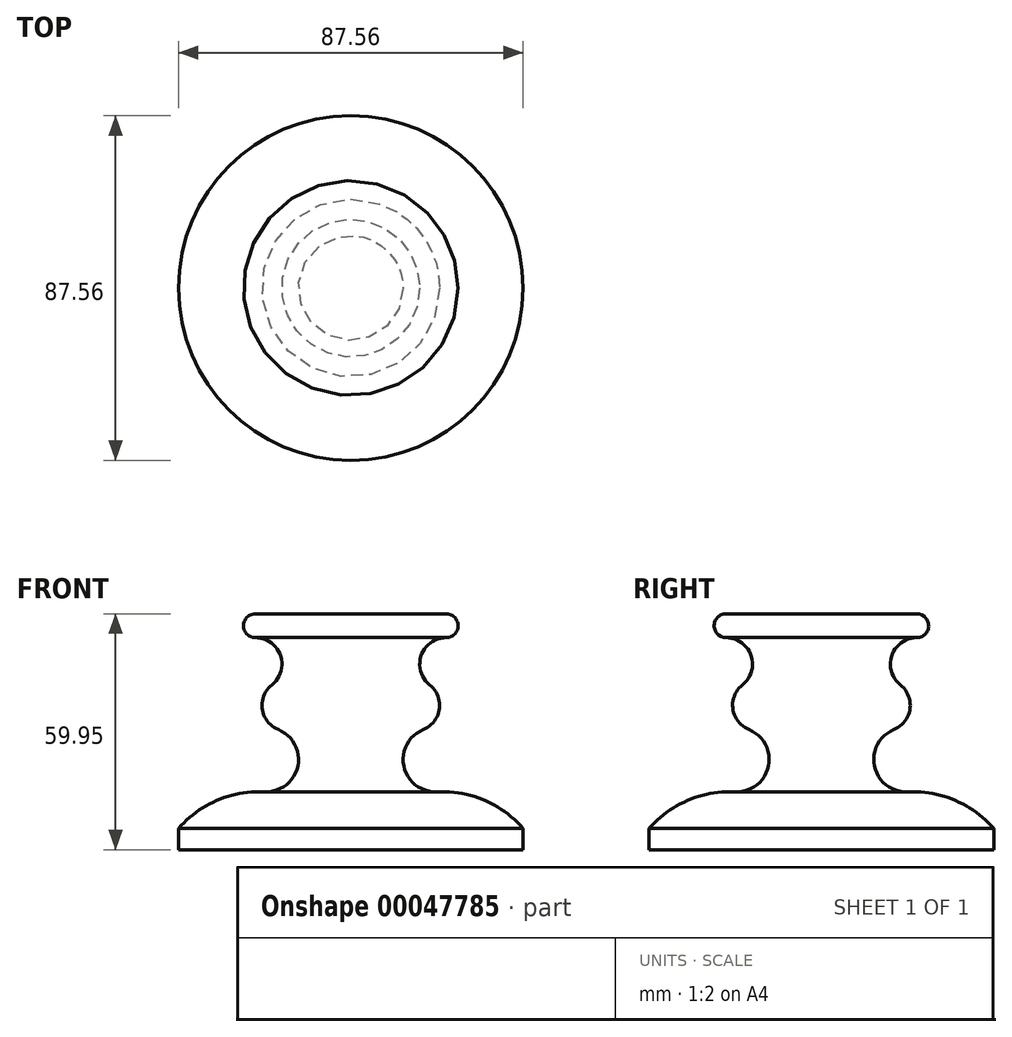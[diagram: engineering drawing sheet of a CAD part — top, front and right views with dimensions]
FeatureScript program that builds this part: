
annotation { "Feature Type Name" : "Feature", "Feature Type Description" : "" }
export const myFeature = defineFeature(function(context is Context, id is Id, definition is map)
    precondition{}
    {
        {
            var Q0;
            Q0=qCreatedBy(makeId("Front.planeOp"),FACE);
            var sketch = newSketch(context, id + "F0", { "sketchPlane" : qUnion([Q0])});
            skLineSegment(sketch, "E0", {"start": v(-24.23, 0) * mm, "end": v(0, 0) * mm});
            skLineSegment(sketch, "E1", {"start": v(0, 0) * mm, "end": v(0, -59.95) * mm});
            skLineSegment(sketch, "E2", {"start": v(0, -59.95) * mm, "end": v(-43.78, -59.95) * mm});
            skLineSegment(sketch, "E3", {"start": v(-43.78, -59.95) * mm, "end": v(-43.78, -54.55) * mm});
            skArc(sketch, "E4", {"start": v(-43.78, -54.55) * mm, "mid": v(-33.92, -47.36) * mm, "end": v(-21.9, -45.2) * mm});
            skArc(sketch, "E5", {"start": v(-21.9, -45.2) * mm, "mid": v(-13.5, -38.78) * mm, "end": v(-18.41, -29.41) * mm});
            skArc(sketch, "E6", {"start": v(-20.05, -18.03) * mm, "mid": v(-17.88, -10.55) * mm, "end": v(-24.23, -6.05) * mm});
            skArc(sketch, "E7", {"start": v(-24.23, -6.05) * mm, "mid": v(-27.25, -3.02) * mm, "end": v(-24.23, 0) * mm});
            skArc(sketch, "E8", {"start": v(-20.05, -18.03) * mm, "mid": v(-22.5, -24.19) * mm, "end": v(-18.41, -29.41) * mm});
            skLineSegment(sketch, "E9", {"start": v(-24.23, -6.05) * mm, "end": v(-5.94, -6.05) * mm, "construction": true});
            skSolve(sketch);
        }
        {
            var Q0;
            Q0 = qSketchRegion(id + "F0", true);
            var Q1;
            Q1=makeQuery(id+"F0.imprint","IMPRINT",FACE,{"disambiguationData":[TD([[makeQuery(id+"F0.imprint","IMPRINT",EDGE,{"derivedFrom":sQuery(id+"F0.wireOp",EDGE,"E0")}),-1.0]])]});
            var Q2;
            Q2=sQuery(id+"F0.wireOp",EDGE,"E1");
            revolve(context, id + "F1", {"entities" : qUnion([Q0, Q1]), "axis" : qUnion([Q2]), "revolveType" : RevolveType.FULL});
        }
    });
